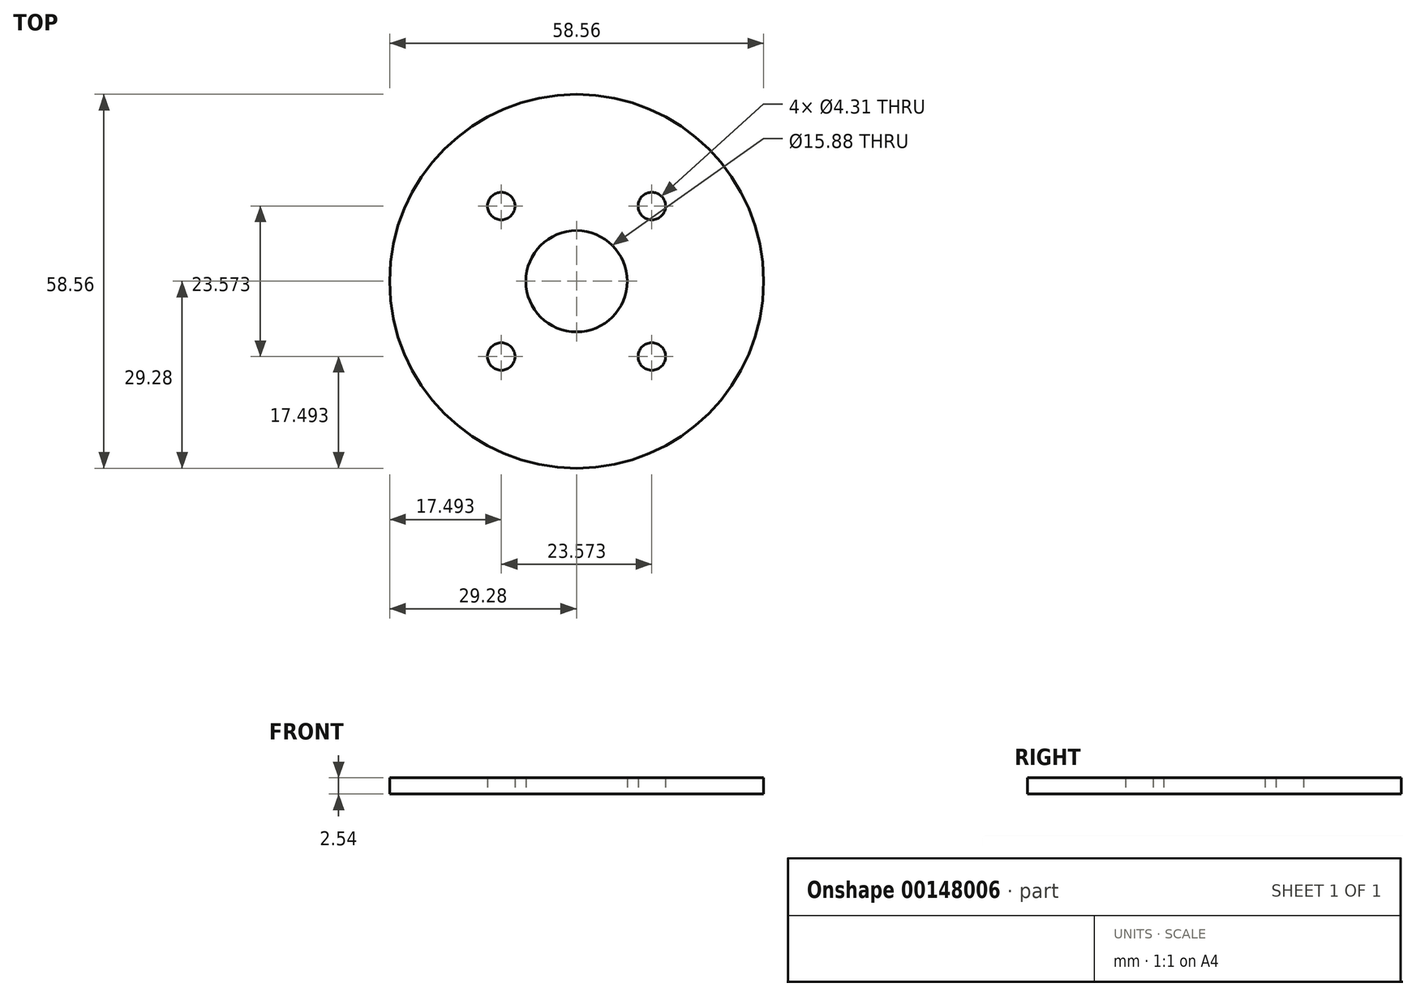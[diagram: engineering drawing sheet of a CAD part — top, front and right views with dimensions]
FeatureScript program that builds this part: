
annotation { "Feature Type Name" : "Feature", "Feature Type Description" : "" }
export const myFeature = defineFeature(function(context is Context, id is Id, definition is map)
    precondition{}
    {
        {
            var Q0;
            Q0=qCreatedBy(makeId("Top.planeOp"),FACE);
            var sketch = newSketch(context, id + "F0", { "sketchPlane" : qUnion([Q0])});
            skCircle(sketch, "E0", {"center": v(0, 0) * mm, "radius": 29.28 * mm});
            skCircle(sketch, "E1", {"center": v(0, 0) * mm, "radius": 7.94 * mm});
            skLineSegment(sketch, "E2.bottom", {"start": v(-11.79, 11.79) * mm, "end": v(11.79, 11.79) * mm, "construction": true});
            skLineSegment(sketch, "E2.top", {"start": v(-11.79, -11.79) * mm, "end": v(11.79, -11.79) * mm, "construction": true});
            skLineSegment(sketch, "E2.left", {"start": v(-11.79, 11.79) * mm, "end": v(-11.79, -11.79) * mm, "construction": true});
            skLineSegment(sketch, "E2.right", {"start": v(11.79, 11.79) * mm, "end": v(11.79, -11.79) * mm, "construction": true});
            skCircle(sketch, "E3", {"center": v(11.79, 11.79) * mm, "radius": 2.15 * mm});
            skCircle(sketch, "E4", {"center": v(-11.79, 11.79) * mm, "radius": 2.15 * mm});
            skCircle(sketch, "E5", {"center": v(-11.79, -11.79) * mm, "radius": 2.15 * mm});
            skCircle(sketch, "E6", {"center": v(11.79, -11.79) * mm, "radius": 2.15 * mm});
            skCircle(sketch, "E7", {"center": v(-11.79, -11.79) * mm, "radius": 3.97 * mm, "construction": true});
            skCircle(sketch, "E8", {"center": v(11.79, 11.79) * mm, "radius": 3.97 * mm, "construction": true});
            skSolve(sketch);
        }
        {
            var Q0;
            Q0=qSketchRegion(id+"F0",true);
            extrude(context, id + "F1", {"entities" : qUnion([Q0]), "depth" : 2.54 * mm});
        }
    });
